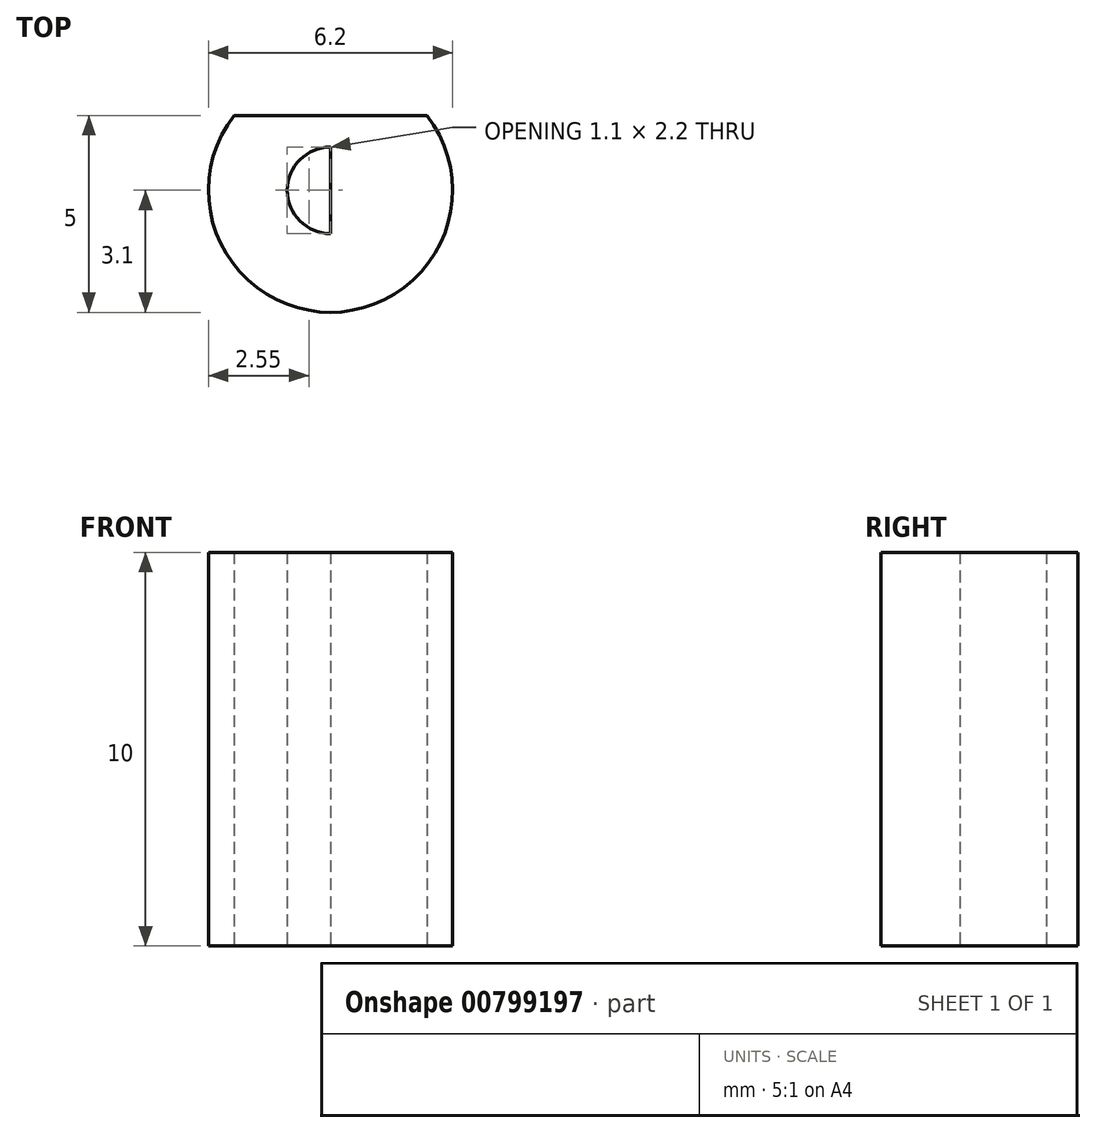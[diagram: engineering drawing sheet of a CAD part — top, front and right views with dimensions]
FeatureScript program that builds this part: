
annotation { "Feature Type Name" : "Feature", "Feature Type Description" : "" }
export const myFeature = defineFeature(function(context is Context, id is Id, definition is map)
    precondition{}
    {
        {
            var Q0;
            Q0=qCreatedBy(makeId("Top.planeOp"),FACE);
            var sketch = newSketch(context, id + "F0", { "sketchPlane" : qUnion([Q0])});
            skCircle(sketch, "E0", {"center": v(0, 0) * mm, "radius": 3.1 * mm});
            skLineSegment(sketch, "E1", {"start": v(0, -3.1) * mm, "end": v(0, 1.9) * mm});
            skLineSegment(sketch, "E2", {"start": v(0, 1.9) * mm, "end": v(2.45, 1.9) * mm});
            skLineSegment(sketch, "E3", {"start": v(2.45, 1.9) * mm, "end": v(-2.45, 1.9) * mm});
            skCircle(sketch, "E4", {"center": v(0, 0) * mm, "radius": 1.1 * mm});
            skLineSegment(sketch, "E5", {"start": v(0, -1.1) * mm, "end": v(0, 0.65) * mm});
            skLineSegment(sketch, "E6", {"start": v(0, 0.65) * mm, "end": v(-0.89, 0.65) * mm});
            skLineSegment(sketch, "E7", {"start": v(-0.89, 0.65) * mm, "end": v(0.89, 0.65) * mm});
            skSolve(sketch);
        }
        {
            var Q0;
            {var subQ0=sQuery(id+"F0.wireOp",EDGE,"E1");Q0=makeQuery(id+"F0.imprint","IMPRINT",FACE,{"disambiguationData":[TD([[makeQuery(id+"F0.imprint","IMPRINT",EDGE,{"derivedFrom":subQ0}),1.0]])]});}
            var Q1;
            {var subQ0=sQuery(id+"F0.wireOp",EDGE,"E1");Q1=makeQuery(id+"F0.imprint","IMPRINT",FACE,{"disambiguationData":[TD([[makeQuery(id+"F0.imprint","IMPRINT",EDGE,{"derivedFrom":subQ0}),-1.0]])]});}
            var Q2;
            {var subQ0=sQuery(id+"F0.wireOp",EDGE,"E7");var subQ3=sQuery(id+"F0.wireOp",EDGE,"E4");var subQ5=makeQuery(id+"F0.imprint","INTERSECT",VERTEX,{"disambiguationData":[OD(0.0)],"derivedFrom":[subQ3,subQ0]});Q2=makeQuery(id+"F0.imprint","IMPRINT",FACE,{"disambiguationData":[TD([[makeQuery(id+"F0.imprint","IMPRINT",EDGE,{"disambiguationData":[TD([[subQ5,1.0]])],"derivedFrom":subQ3}),1.0]])]});}
            var Q3;
            {var subQ0=sQuery(id+"F0.wireOp",EDGE,"E7");var subQ3=sQuery(id+"F0.wireOp",EDGE,"E4");var subQ5=makeQuery(id+"F0.imprint","INTERSECT",VERTEX,{"disambiguationData":[OD(1.0)],"derivedFrom":[subQ3,subQ0]});Q3=makeQuery(id+"F0.imprint","IMPRINT",FACE,{"disambiguationData":[TD([[makeQuery(id+"F0.imprint","IMPRINT",EDGE,{"disambiguationData":[TD([[subQ5,-1.0]])],"derivedFrom":subQ3}),1.0]])]});}
            extrude(context, id + "F1", {"entities" : qUnion([Q0, Q1, Q2, Q3]), "depth" : 10 * mm, "offsetDistance" : 25 * mm});
        }
        {
            var Q0;
            {var subQ0=sQuery(id+"F0.wireOp",EDGE,"E3");var subQ1=sQuery(id+"F0.wireOp",EDGE,"E0");var subQ2=makeQuery(id+"F0.imprint","INTERSECT",VERTEX,{"disambiguationData":[OD(0.0)],"derivedFrom":[subQ1,subQ0]});Q0=makeQuery(id+"F0.imprint","IMPRINT",FACE,{"disambiguationData":[TD([[makeQuery(id+"F0.imprint","IMPRINT",EDGE,{"disambiguationData":[TD([[subQ2,-1.0]])],"derivedFrom":subQ1}),1.0]])]});}
            extrude(context, id + "F2", {"entities" : qUnion([Q0]), "operationType" : NewBodyOperationType.ADD, "depth" : 4.7 * mm, "offsetDistance" : 25 * mm});
        }
    });
